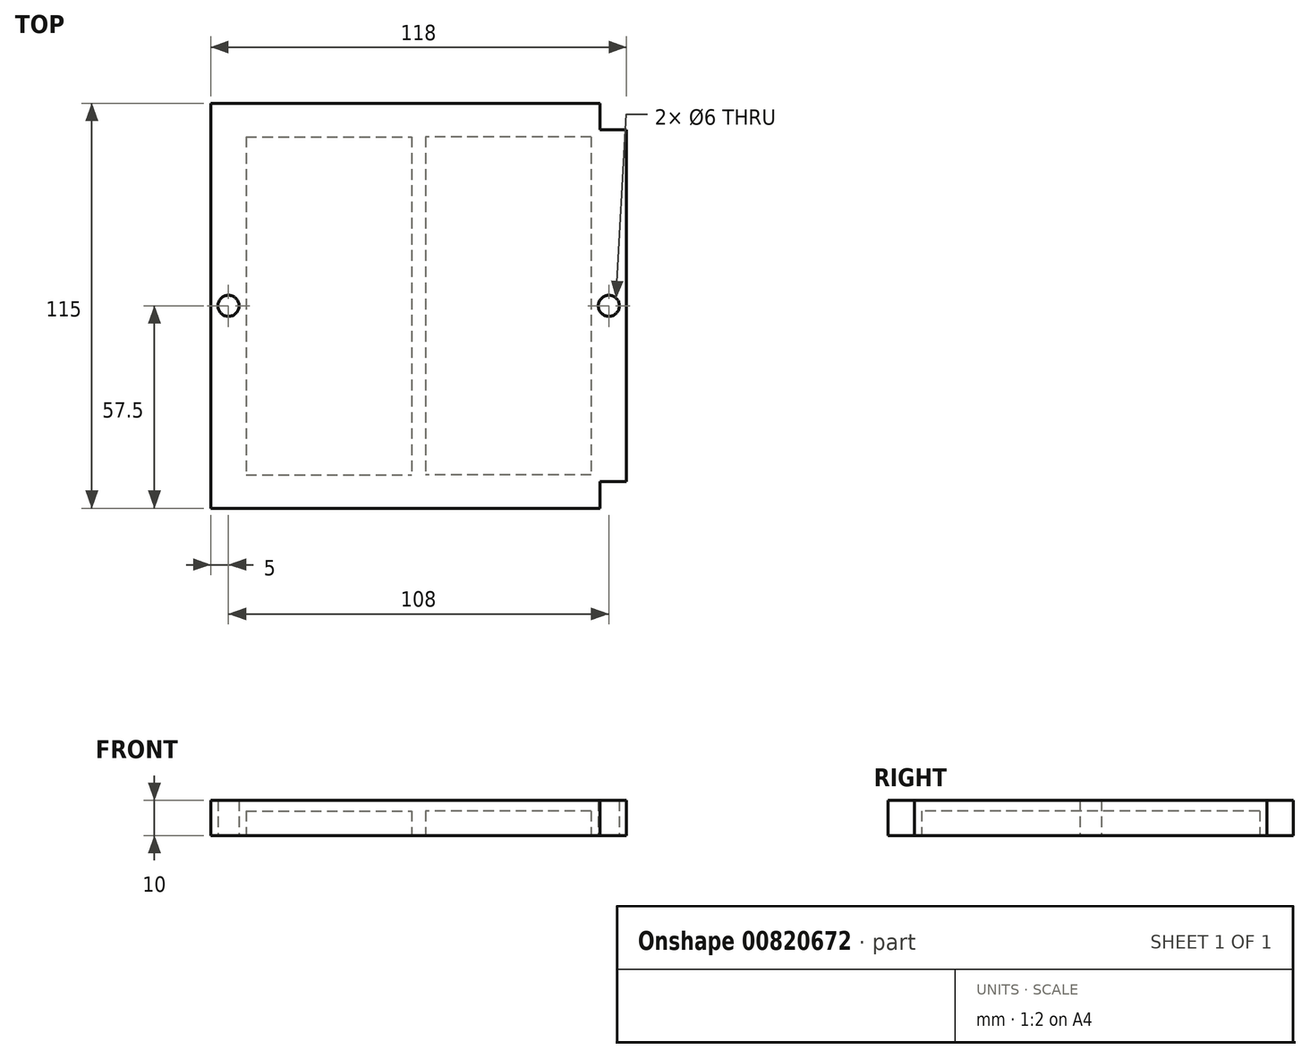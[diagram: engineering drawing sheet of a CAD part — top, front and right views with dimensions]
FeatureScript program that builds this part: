
annotation { "Feature Type Name" : "Feature", "Feature Type Description" : "" }
export const myFeature = defineFeature(function(context is Context, id is Id, definition is map)
    precondition{}
    {
        {
            var Q0;
            Q0=qCreatedBy(makeId("Top.planeOp"),FACE);
            var sketch = newSketch(context, id + "F0", { "sketchPlane" : qUnion([Q0])});
            skLineSegment(sketch, "E0.bottom", {"start": v(-59, -57.5) * mm, "end": v(59, -57.5) * mm});
            skLineSegment(sketch, "E0.top", {"start": v(-59, 57.5) * mm, "end": v(59, 57.5) * mm});
            skLineSegment(sketch, "E0.left", {"start": v(-59, -57.5) * mm, "end": v(-59, 57.5) * mm});
            skLineSegment(sketch, "E0.right", {"start": v(59, -57.5) * mm, "end": v(59, 57.5) * mm});
            skLineSegment(sketch, "E1.MirrorCS", {"start": v(-49, 144) * mm, "end": v(-2, 144) * mm});
            skCircle(sketch, "E2", {"center": v(-54, 0) * mm, "radius": 3 * mm});
            skPoint(sketch, "E2.centerSnap0", {"position": v(-59, 0) * mm});
            skCircle(sketch, "E3", {"center": v(54, 0) * mm, "radius": 3 * mm});
            skPoint(sketch, "E4", {"position": v(59, -57.5) * mm});
            skPoint(sketch, "E5", {"position": v(0, -57.5) * mm});
            skPoint(sketch, "E6", {"position": v(59, 0) * mm});
            skSolve(sketch);
        }
        {
            var Q0;
            Q0=qCreatedBy(makeId("Top.planeOp"),FACE);
            var sketch = newSketch(context, id + "F1", { "sketchPlane" : qUnion([Q0])});
            skLineSegment(sketch, "E7.bottom", {"start": v(-49, 48) * mm, "end": v(-2, 48) * mm});
            skLineSegment(sketch, "E7.top", {"start": v(-49, -48) * mm, "end": v(-2, -48) * mm});
            skLineSegment(sketch, "E7.left", {"start": v(-49, 48) * mm, "end": v(-49, -48) * mm});
            skLineSegment(sketch, "E7.right", {"start": v(-2, 48) * mm, "end": v(-2, -48) * mm});
            skLineSegment(sketch, "E8.MirrorCS", {"start": v(-49, 144) * mm, "end": v(-2, 144) * mm});
            skLineSegment(sketch, "E9.MirrorCS", {"start": v(49, 48) * mm, "end": v(49, -48) * mm});
            skLineSegment(sketch, "E10.MirrorCS", {"start": v(49, 48) * mm, "end": v(2, 48) * mm});
            skLineSegment(sketch, "E11.MirrorCS", {"start": v(2, 48) * mm, "end": v(2, -48) * mm});
            skLineSegment(sketch, "E12.MirrorCS", {"start": v(49, -48) * mm, "end": v(2, -48) * mm});
            skSolve(sketch);
        }
        {
            var Q0;
            Q0 = qSketchRegion(id + "F0", true);
            extrude(context, id + "F2", {"entities" : qUnion([Q0]), "depth" : 10 * mm, "offsetDistance" : 25 * mm});
        }
        {
            var Q0;
            Q0 = qSketchRegion(id + "F1", true);
            extrude(context, id + "F3", {"entities" : qUnion([Q0]), "operationType" : NewBodyOperationType.REMOVE, "depth" : 7 * mm, "offsetDistance" : 25 * mm});
        }
        {
            var Q0;
            Q0=qCreatedBy(makeId("Top.planeOp"),FACE);
            var sketch = newSketch(context, id + "F4", { "sketchPlane" : qUnion([Q0])});
            skLineSegment(sketch, "E13.bottom", {"start": v(59, -57.5) * mm, "end": v(51.5, -57.5) * mm});
            skLineSegment(sketch, "E13.top", {"start": v(59, -50) * mm, "end": v(51.5, -50) * mm});
            skLineSegment(sketch, "E13.left", {"start": v(59, -57.5) * mm, "end": v(59, -50) * mm});
            skLineSegment(sketch, "E13.right", {"start": v(51.5, -57.5) * mm, "end": v(51.5, -50) * mm});
            skLineSegment(sketch, "E14.MirrorCS", {"start": v(59, 50) * mm, "end": v(51.5, 50) * mm});
            skLineSegment(sketch, "E15.MirrorCS", {"start": v(51.5, 57.5) * mm, "end": v(51.5, 50) * mm});
            skLineSegment(sketch, "E16.MirrorCS", {"start": v(59, 57.5) * mm, "end": v(51.5, 57.5) * mm});
            skLineSegment(sketch, "E17.MirrorCS", {"start": v(59, 57.5) * mm, "end": v(59, 50) * mm});
            skSolve(sketch);
        }
        {
            var Q0;
            Q0 = qSketchRegion(id + "F4", true);
            extrude(context, id + "F5", {"entities" : qUnion([Q0]), "operationType" : NewBodyOperationType.REMOVE, "depth" : 25 * mm, "offsetDistance" : 25 * mm});
        }
    });
